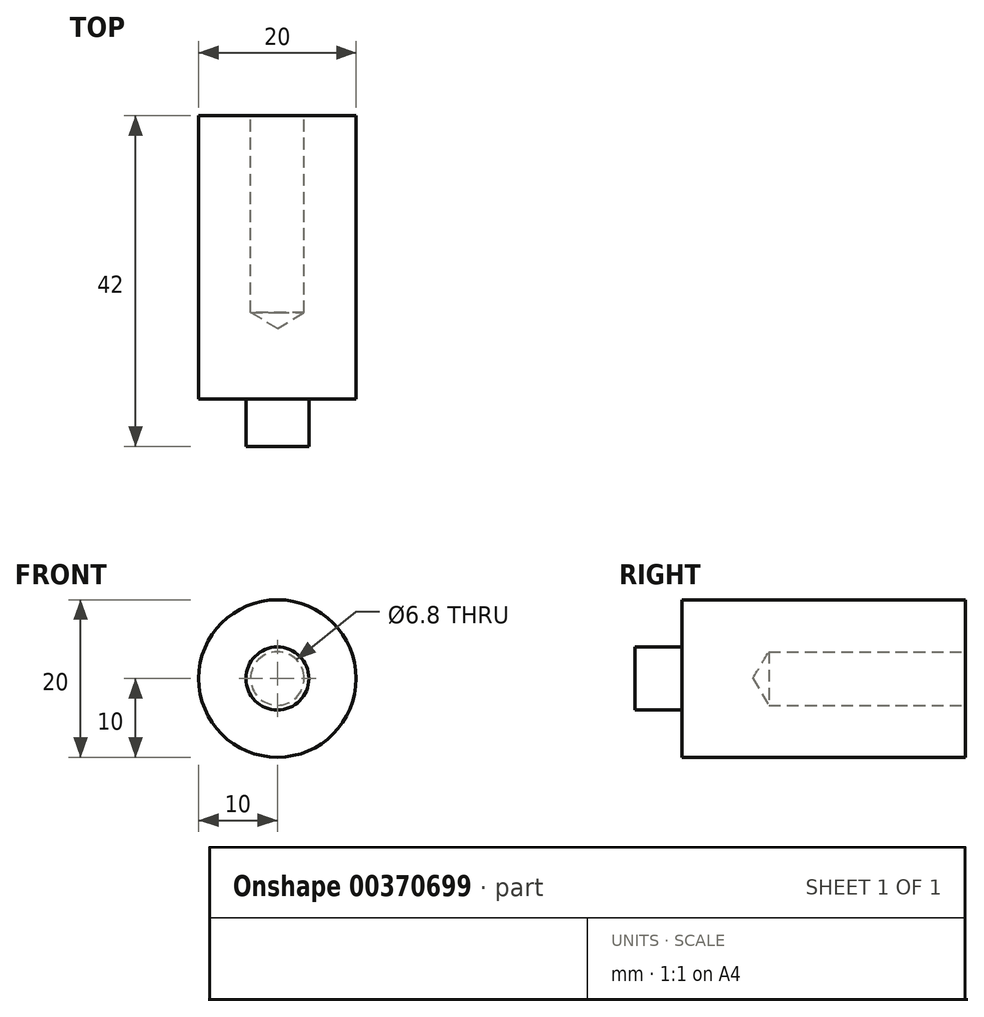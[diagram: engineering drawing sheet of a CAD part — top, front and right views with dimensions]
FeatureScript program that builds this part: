
annotation { "Feature Type Name" : "Feature", "Feature Type Description" : "" }
export const myFeature = defineFeature(function(context is Context, id is Id, definition is map)
    precondition{}
    {
        {
            var Q0;
            Q0=qCreatedBy(makeId("Front.planeOp"),FACE);
            var sketch = newSketch(context, id + "F0", { "sketchPlane" : qUnion([Q0])});
            skCircle(sketch, "E0", {"center": v(0, 0) * mm, "radius": 10 * mm});
            skSolve(sketch);
        }
        {
            var Q0;
            Q0 = qSketchRegion(id + "F0", true);
            extrude(context, id + "F1", {"entities" : qUnion([Q0]), "oppositeDirection" : true, "depth" : 42 * mm});
        }
        {
            var Q0;
            Q0=makeQuery(id+"F1.opExtrude","CAP_FACE",FACE,{"disambiguationData":[OSD([sQuery(id+"F0.wireOp",EDGE,"E0")])],"isStart":true});
            var sketch = newSketch(context, id + "F2", { "sketchPlane" : qUnion([Q0])});
            skCircle(sketch, "E1", {"center": v(0, 0) * mm, "radius": 16.47 * mm});
            skCircle(sketch, "E2", {"center": v(0, 0) * mm, "radius": 4 * mm});
            skSolve(sketch);
        }
        {
            var Q0;
            Q0 = qSketchRegion(id + "F2", true);
            extrude(context, id + "F3", {"entities" : qUnion([Q0]), "operationType" : NewBodyOperationType.REMOVE, "oppositeDirection" : true, "depth" : 6 * mm});
        }
        {
            var Q0;
            Q0=makeQuery(id+"F1.opExtrude","CAP_FACE",FACE,{"disambiguationData":[OSD([sQuery(id+"F0.wireOp",EDGE,"E0")])],"isStart":false});
            var sketch = newSketch(context, id + "F4", { "sketchPlane" : qUnion([Q0])});
            skCircle(sketch, "E3", {"center": v(0, 0) * mm, "radius": 3.4 * mm});
            skSolve(sketch);
        }
        {
            var Q0;
            Q0=sQuery(id+"F4.wireOp",VERTEX,"E3.center");
            var Q1;
            Q1=makeQuery(id+"F1.opExtrude","SWEPT_BODY",BODY,{"disambiguationData":[OSD([sQuery(id+"F0.wireOp",EDGE,"E0")])]});
            hole(context, id + "F5", {"style" : HoleStyle.SIMPLE, "endStyle" : HoleEndStyle.BLIND, "holeDiameter" : 6.8 * mm, "holeDepth" : 25 * mm, "isTappedThrough" : true, "tappedDepth" : 12 * mm, "tapClearance" : 3, "locations" : qUnion([Q0]), "scope" : qUnion([Q1])});
        }
    });
